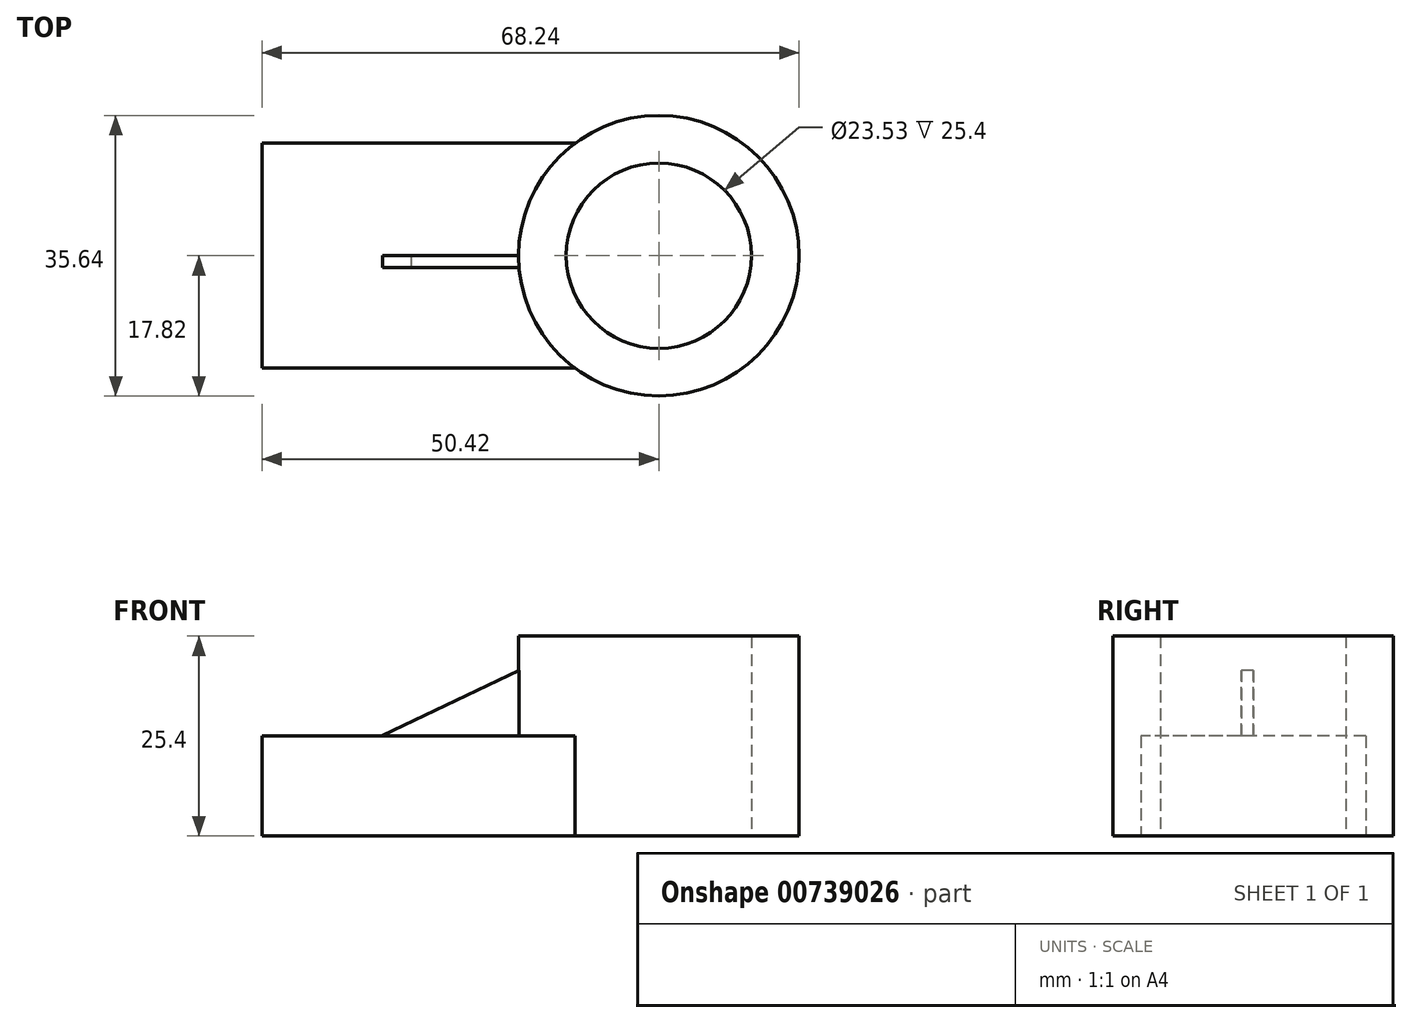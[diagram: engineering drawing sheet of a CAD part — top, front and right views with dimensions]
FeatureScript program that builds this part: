
annotation { "Feature Type Name" : "Feature", "Feature Type Description" : "" }
export const myFeature = defineFeature(function(context is Context, id is Id, definition is map)
    precondition{}
    {
        {
            var Q0;
            Q0=qCreatedBy(makeId("Top.planeOp"),FACE);
            var sketch = newSketch(context, id + "F0", { "sketchPlane" : qUnion([Q0])});
            skCircle(sketch, "E0", {"center": v(0, 0) * mm, "radius": 17.82 * mm});
            skSolve(sketch);
        }
        {
            var Q0;
            Q0 = qSketchRegion(id + "F0", true);
            extrude(context, id + "F1", {"entities" : qUnion([Q0]), "depth" : 25.4 * mm, "offsetDistance" : 25.4 * mm});
        }
        {
            var Q0;
            Q0=qCreatedBy(makeId("Top.planeOp"),FACE);
            var sketch = newSketch(context, id + "F2", { "sketchPlane" : qUnion([Q0])});
            skLineSegment(sketch, "E1.bottom", {"start": v(0, 14.29) * mm, "end": v(-50.42, 14.29) * mm});
            skLineSegment(sketch, "E1.top", {"start": v(0, -14.29) * mm, "end": v(-50.42, -14.29) * mm});
            skLineSegment(sketch, "E1.left", {"start": v(0, 14.29) * mm, "end": v(0, -14.29) * mm});
            skLineSegment(sketch, "E1.right", {"start": v(-50.42, 14.29) * mm, "end": v(-50.42, -14.29) * mm});
            skSolve(sketch);
        }
        {
            var Q0;
            Q0 = qSketchRegion(id + "F2", true);
            extrude(context, id + "F3", {"entities" : qUnion([Q0]), "operationType" : NewBodyOperationType.ADD, "depth" : 12.7 * mm, "offsetDistance" : 25.4 * mm});
        }
        {
            var Q0;
            Q0=qCreatedBy(makeId("Top.planeOp"),FACE);
            var sketch = newSketch(context, id + "F4", { "sketchPlane" : qUnion([Q0])});
            skCircle(sketch, "E2", {"center": v(0, 0) * mm, "radius": 11.76 * mm});
            skSolve(sketch);
        }
        {
            var Q0;
            Q0 = qSketchRegion(id + "F4", true);
            extrude(context, id + "F5", {"entities" : qUnion([Q0]), "operationType" : NewBodyOperationType.REMOVE, "depth" : 25.4 * mm, "offsetDistance" : 25.4 * mm});
        }
        {
            var Q0;
            Q0=qCreatedBy(makeId("Front.planeOp"),FACE);
            var sketch = newSketch(context, id + "F6", { "sketchPlane" : qUnion([Q0])});
            skLineSegment(sketch, "E3", {"start": v(-35.12, 12.81) * mm, "end": v(-17.24, 21.3) * mm});
            skLineSegment(sketch, "E4", {"start": v(-17.24, 21.3) * mm, "end": v(-17.24, 12.26) * mm});
            skLineSegment(sketch, "E5", {"start": v(-17.24, 12.26) * mm, "end": v(-35.12, 12.81) * mm});
            skSolve(sketch);
        }
        {
            var Q0;
            Q0 = qSketchRegion(id + "F6", true);
            extrude(context, id + "F7", {"entities" : qUnion([Q0]), "operationType" : NewBodyOperationType.ADD, "depth" : 1.52 * mm, "offsetDistance" : 25.4 * mm});
        }
    });
